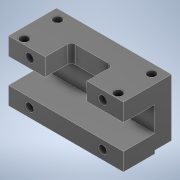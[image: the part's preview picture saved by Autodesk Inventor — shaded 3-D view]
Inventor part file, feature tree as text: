
AUTODESK INVENTOR PART (.ipt)
format: ipt  version: 2021 (Build 250183000, 183)  size: 205,824 bytes
history: native  units: mm
features: sketch x8, other x6, extrude x5, hole x3, fillet x1
ambient origin geometry x8: Origin, YZ Plane, XZ Plane, XY Plane, X Axis, Y Axis, Z Axis, Center Point
bodies: Body1 (feature_tree)
feature tree (23):
  other  "Sólido1"
  extrude  "Extrusão1"  Depth=23.0mm
  extrude  "Extrusão2"  Depth=8.0mm
  extrude  "Extrusão3"  Depth=15.0mm
  extrude  "Extrusão4"  Depth=8.5mm
  hole  "Furo1"  [1 undecoded]
  extrude  "Extrusão5"  Depth=27.5mm
  fillet  "Arredondamento1"  Radius=27.5mm
  hole  "Furo3"  [1 undecoded]
  other  "Plano de trabalho2"
  hole  "Furo4"  [1 undecoded]
  sketch  "Esboço1"  dims[d0=35.0mm d1=23.0mm]
  sketch  "Esboço2"  dims[d2=55.0mm d3=0.0mm d4=8.0mm]
  sketch  "Esboço3"  dims[d5=1.5mm d6=0.0mm d7=15.0mm]
  sketch  "Esboço4"  dims[d8=12.0mm d9=8.5mm]
  sketch  "Esboço5"  dims[d10=0.0mm d11=0.0mm d12=8.5mm]
  other  "Contorno projetado1"
  sketch  "Esboço6"  dims[d13=0.0mm d14=0.0mm d15=4.0mm d16=27.5mm]
  sketch  "Esboço8"  dims[d17=10.0mm d18=10.0mm]
  other  "Contorno projetado4"
  sketch  "Esboço9"  dims[d19=4.0mm d20=6.0mm d21=4.0mm d22=2.0mm d23=90.0deg d24=5.0mm d25=0.0mm d26=20.0mm d27=12.5mm d28=27.5mm d30=2.0mm d31=0.0mm d32=2.0mm d45=2.5mm d46=4.5mm d47=5.0mm d48=5.0mm d49=4.0mm d50=6.0mm d51=4.0mm d52=2.0mm d53=90.0deg d54=5.0mm d55=0.0mm d56=4.25mm d57=10.0mm d58=4.25mm d59=10.0mm d60=4.0mm d61=6.0mm d62=6.0mm d63=2.0mm d64=90.0deg d65=5.0mm d66=0.0mm]
  other  "Contorno projetado5"
  other  "Contorno projetado6"
note: 3 required parameter values undecoded (feature->parameter linkage not recoverable at this tier; creation-order binding heuristic only, values carry confidence <= 0.55)
